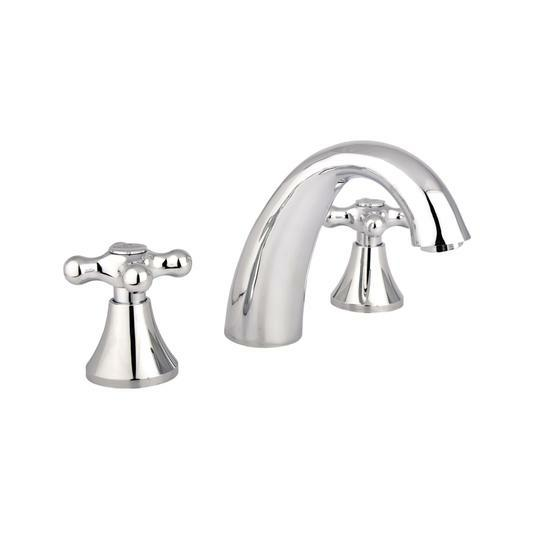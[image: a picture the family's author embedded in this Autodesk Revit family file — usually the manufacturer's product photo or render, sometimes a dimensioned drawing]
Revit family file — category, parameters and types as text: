
# Revit family: 01-0812-11 MEZCLADOR LAVAMANOS 8” CALIMA
name_source: partatom
category: Plumbing Fixtures
revit_build: Autodesk Revit 2018 (Build: 20170223_1515(x64)
units: mm (PartAtom-declared; Revit-internal decimal feet)

## family parameters
Cut with Voids When Loaded = No
Host = Face
OmniClass Number = 23.31.11.00
Part Type = Normal
Room Calculation Point = No
Round Connector Dimension = Use Diameter
Shared = No

## types (1)
- 01-0812-11
    Alto - Aireador = 110 mm  [stored 0.360892 ft]
    Alto manija = 68.2 mm
    Ancho manija = 69 mm
    CW Connection = Yes
    Default Elevation = 0 mm  [stored 0 ft]
    Description = Bimando baño
    Eje - Rosca = 203.2 mm  [stored 0.666667 ft]
    Eje-Aireador = 124 mm
    Escudo = 50 mm  [stored 0.164042 ft]
    HW Connection = Yes
    Link ficha tecnica = http://infotecnica.gricol.com
    Manufacturer = Gricol
    Metal Laton Cromado = Metal Laton Cromado
    Model = 01-0812-11
    Plastico ABS Cromado = Plastico - ABS Cromado
    Product Name = MEZCLADOR LAVAMANOS 8” CALIMA
    Type Image = MEZCLADOR LAVAMANOS 8” CALIMA.jpg
    URL = https://www.gricol.com
    Vent Connection = No
    Waste Connection = No

note: [stored X ft] marks values corroborated as IEEE doubles in the binary element streams (Revit-internal decimal feet)

## geometry (parser evidence)
native form markers: Blend x2, Sweep x7
no freeform markers — native parametric forms only
